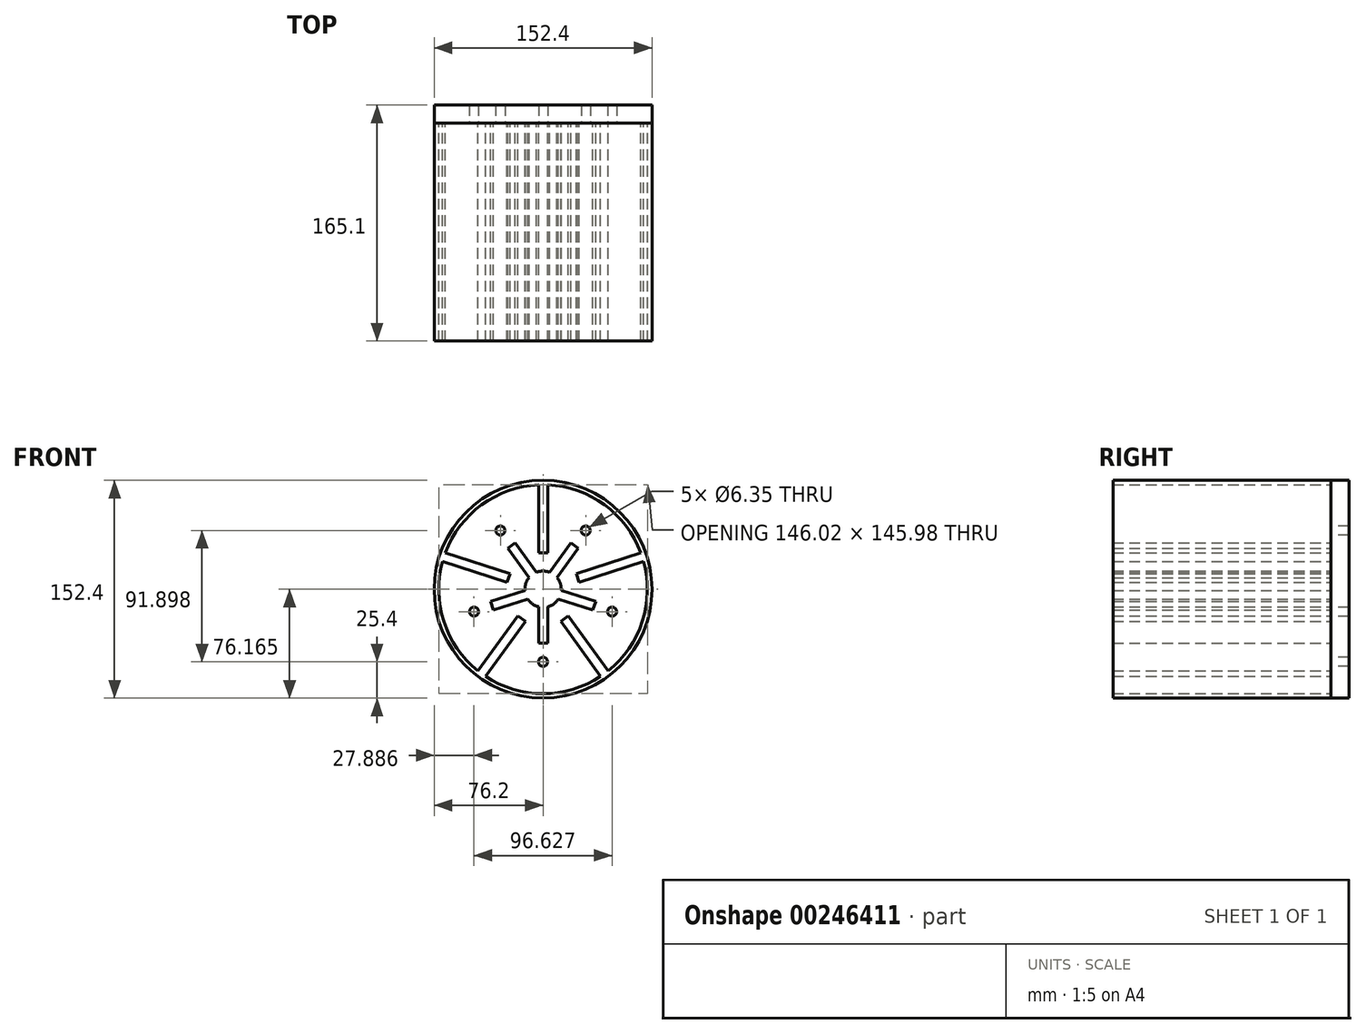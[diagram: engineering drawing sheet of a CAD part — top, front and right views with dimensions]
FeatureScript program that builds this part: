
annotation { "Feature Type Name" : "Feature", "Feature Type Description" : "" }
export const myFeature = defineFeature(function(context is Context, id is Id, definition is map)
    precondition{}
    {
        {
            var Q0;
            Q0=qCreatedBy(makeId("Front.planeOp"),FACE);
            var sketch = newSketch(context, id + "F0", { "sketchPlane" : qUnion([Q0])});
            skCircle(sketch, "E0", {"center": v(0, 0) * mm, "radius": 76.2 * mm});
            skArc(sketch, "E1", {"start": v(-40.31, -60.89) * mm, "mid": v(0, -73.03) * mm, "end": v(40.31, -60.89) * mm});
            skLineSegment(sketch, "E2", {"start": v(0, 0) * mm, "end": v(0, 76.2) * mm, "construction": true});
            skLineSegment(sketch, "E3", {"start": v(-76.2, 0) * mm, "end": v(76.2, 0) * mm, "construction": true});
            skLineSegment(sketch, "E4", {"start": v(-3.17, 25.4) * mm, "end": v(-3.18, 72.96) * mm});
            skLineSegment(sketch, "E5", {"start": v(3.18, 25.4) * mm, "end": v(3.17, 72.96) * mm});
            skLineSegment(sketch, "E6", {"start": v(-3.17, 25.4) * mm, "end": v(3.18, 25.4) * mm});
            skLineSegment(sketch, "E7.1.0", {"start": v(-25.14, 4.83) * mm, "end": v(-70.37, 19.53) * mm});
            skLineSegment(sketch, "E7.1.1", {"start": v(-23.18, 10.87) * mm, "end": v(-68.4, 25.56) * mm});
            skLineSegment(sketch, "E7.1.2", {"start": v(-25.14, 4.83) * mm, "end": v(-23.18, 10.87) * mm});
            skLineSegment(sketch, "E7.2.0", {"start": v(-12.36, -22.42) * mm, "end": v(-40.31, -60.89) * mm});
            skLineSegment(sketch, "E7.2.1", {"start": v(-17.5, -18.68) * mm, "end": v(-45.45, -57.16) * mm});
            skLineSegment(sketch, "E7.2.2", {"start": v(-12.36, -22.42) * mm, "end": v(-17.5, -18.68) * mm});
            skLineSegment(sketch, "E7.3.0", {"start": v(17.5, -18.68) * mm, "end": v(45.45, -57.16) * mm});
            skLineSegment(sketch, "E7.3.1", {"start": v(12.36, -22.42) * mm, "end": v(40.31, -60.89) * mm});
            skLineSegment(sketch, "E7.3.2", {"start": v(17.5, -18.68) * mm, "end": v(12.36, -22.42) * mm});
            skLineSegment(sketch, "E7.4.0", {"start": v(23.18, 10.87) * mm, "end": v(68.4, 25.56) * mm});
            skLineSegment(sketch, "E7.4.1", {"start": v(25.14, 4.83) * mm, "end": v(70.37, 19.53) * mm});
            skLineSegment(sketch, "E7.4.2", {"start": v(23.18, 10.87) * mm, "end": v(25.14, 4.83) * mm});
            skArc(sketch, "E8", {"start": v(-10.71, -6.82) * mm, "mid": v(-7.46, -10.27) * mm, "end": v(-3.18, -12.3) * mm});
            skLineSegment(sketch, "E9", {"start": v(0, 0) * mm, "end": v(42.92, 59.08) * mm, "construction": true});
            skLineSegment(sketch, "E10", {"start": v(4.66, 11.81) * mm, "end": v(19.59, 32.36) * mm});
            skLineSegment(sketch, "E11", {"start": v(19.59, 32.36) * mm, "end": v(24.73, 28.63) * mm});
            skLineSegment(sketch, "E12", {"start": v(24.73, 28.63) * mm, "end": v(9.8, 8.08) * mm});
            skLineSegment(sketch, "E13.1.0", {"start": v(-19.59, 32.36) * mm, "end": v(-4.66, 11.81) * mm});
            skLineSegment(sketch, "E13.1.1", {"start": v(-24.73, 28.63) * mm, "end": v(-19.59, 32.36) * mm});
            skLineSegment(sketch, "E13.1.2", {"start": v(-9.8, 8.08) * mm, "end": v(-24.73, 28.63) * mm});
            skLineSegment(sketch, "E13.2.0", {"start": v(-36.83, -8.63) * mm, "end": v(-12.68, -0.78) * mm});
            skLineSegment(sketch, "E13.2.1", {"start": v(-34.87, -14.67) * mm, "end": v(-36.83, -8.63) * mm});
            skLineSegment(sketch, "E13.2.2", {"start": v(-10.71, -6.82) * mm, "end": v(-34.87, -14.67) * mm});
            skLineSegment(sketch, "E13.3.0", {"start": v(-3.17, -37.7) * mm, "end": v(-3.18, -12.3) * mm});
            skLineSegment(sketch, "E13.3.1", {"start": v(3.18, -37.7) * mm, "end": v(-3.17, -37.7) * mm});
            skLineSegment(sketch, "E13.3.2", {"start": v(3.17, -12.3) * mm, "end": v(3.18, -37.7) * mm});
            skLineSegment(sketch, "E13.4.0", {"start": v(34.87, -14.67) * mm, "end": v(10.71, -6.82) * mm});
            skLineSegment(sketch, "E13.4.1", {"start": v(36.83, -8.63) * mm, "end": v(34.87, -14.67) * mm});
            skLineSegment(sketch, "E13.4.2", {"start": v(12.68, -0.78) * mm, "end": v(36.83, -8.63) * mm});
            skArc(sketch, "E14.trimOffspring", {"start": v(-9.8, 8.08) * mm, "mid": v(-12.08, 3.92) * mm, "end": v(-12.68, -0.78) * mm});
            skArc(sketch, "E15.trimOffspring", {"start": v(4.66, 11.81) * mm, "mid": v(0, 12.7) * mm, "end": v(-4.66, 11.81) * mm});
            skArc(sketch, "E16.trimOffspring", {"start": v(12.68, -0.78) * mm, "mid": v(12.08, 3.92) * mm, "end": v(9.8, 8.08) * mm});
            skArc(sketch, "E17.trimOffspring", {"start": v(3.17, -12.3) * mm, "mid": v(7.46, -10.27) * mm, "end": v(10.71, -6.82) * mm});
            skArc(sketch, "E18.trimOffspring", {"start": v(45.45, -57.16) * mm, "mid": v(69.45, -22.57) * mm, "end": v(70.37, 19.53) * mm});
            skArc(sketch, "E19.trimOffspring", {"start": v(68.4, 25.56) * mm, "mid": v(42.92, 59.08) * mm, "end": v(3.18, 72.96) * mm});
            skArc(sketch, "E20.trimOffspring", {"start": v(-70.37, 19.53) * mm, "mid": v(-69.45, -22.57) * mm, "end": v(-45.45, -57.16) * mm});
            skArc(sketch, "E21.trimOffspring", {"start": v(-3.18, 72.96) * mm, "mid": v(-42.92, 59.08) * mm, "end": v(-68.4, 25.56) * mm});
            skSolve(sketch);
        }
        {
            var Q0;
            Q0=makeQuery(id+"F0.imprint","IMPRINT",FACE,{"disambiguationData":[TD([[makeQuery(id+"F0.imprint","IMPRINT",EDGE,{"derivedFrom":sQuery(id+"F0.wireOp",EDGE,"E0")}),1.0]])]});
            extrude(context, id + "F1", {"entities" : qUnion([Q0]), "depth" : 152.4 * mm});
        }
        {
            var Q0;
            Q0=makeQuery(id+"F0.imprint","IMPRINT",FACE,{"disambiguationData":[TD([[makeQuery(id+"F0.imprint","IMPRINT",EDGE,{"derivedFrom":sQuery(id+"F0.wireOp",EDGE,"E8")}),1.0]])]});
            extrude(context, id + "F2", {"entities" : qUnion([Q0]), "depth" : 152.4 * mm});
        }
        {
            var Q0;
            Q0=makeQuery(id+"F0.imprint","IMPRINT",FACE,{"disambiguationData":[TD([[makeQuery(id+"F0.imprint","IMPRINT",EDGE,{"derivedFrom":sQuery(id+"F0.wireOp",EDGE,"E8")}),1.0]])]});
            var sketch = newSketch(context, id + "F3", { "sketchPlane" : qUnion([Q0])});
            skCircle(sketch, "E22", {"center": v(0, 0) * mm, "radius": 76.2 * mm});
            skCircle(sketch, "E23", {"center": v(29.86, 41.1) * mm, "radius": 3.18 * mm});
            skCircle(sketch, "E24.1.0", {"center": v(-29.86, 41.1) * mm, "radius": 3.18 * mm});
            skCircle(sketch, "E24.2.0", {"center": v(-48.31, -15.7) * mm, "radius": 3.18 * mm});
            skCircle(sketch, "E25.1.3.0", {"center": v(0, -50.8) * mm, "radius": 3.18 * mm});
            skCircle(sketch, "E25.1.4.0", {"center": v(48.31, -15.7) * mm, "radius": 3.18 * mm});
            skSolve(sketch);
        }
        {
            var Q0;
            Q0 = qSketchRegion(id + "F3", true);
            extrude(context, id + "F4", {"entities" : qUnion([Q0]), "oppositeDirection" : true, "depth" : 12.7 * mm});
        }
    });
